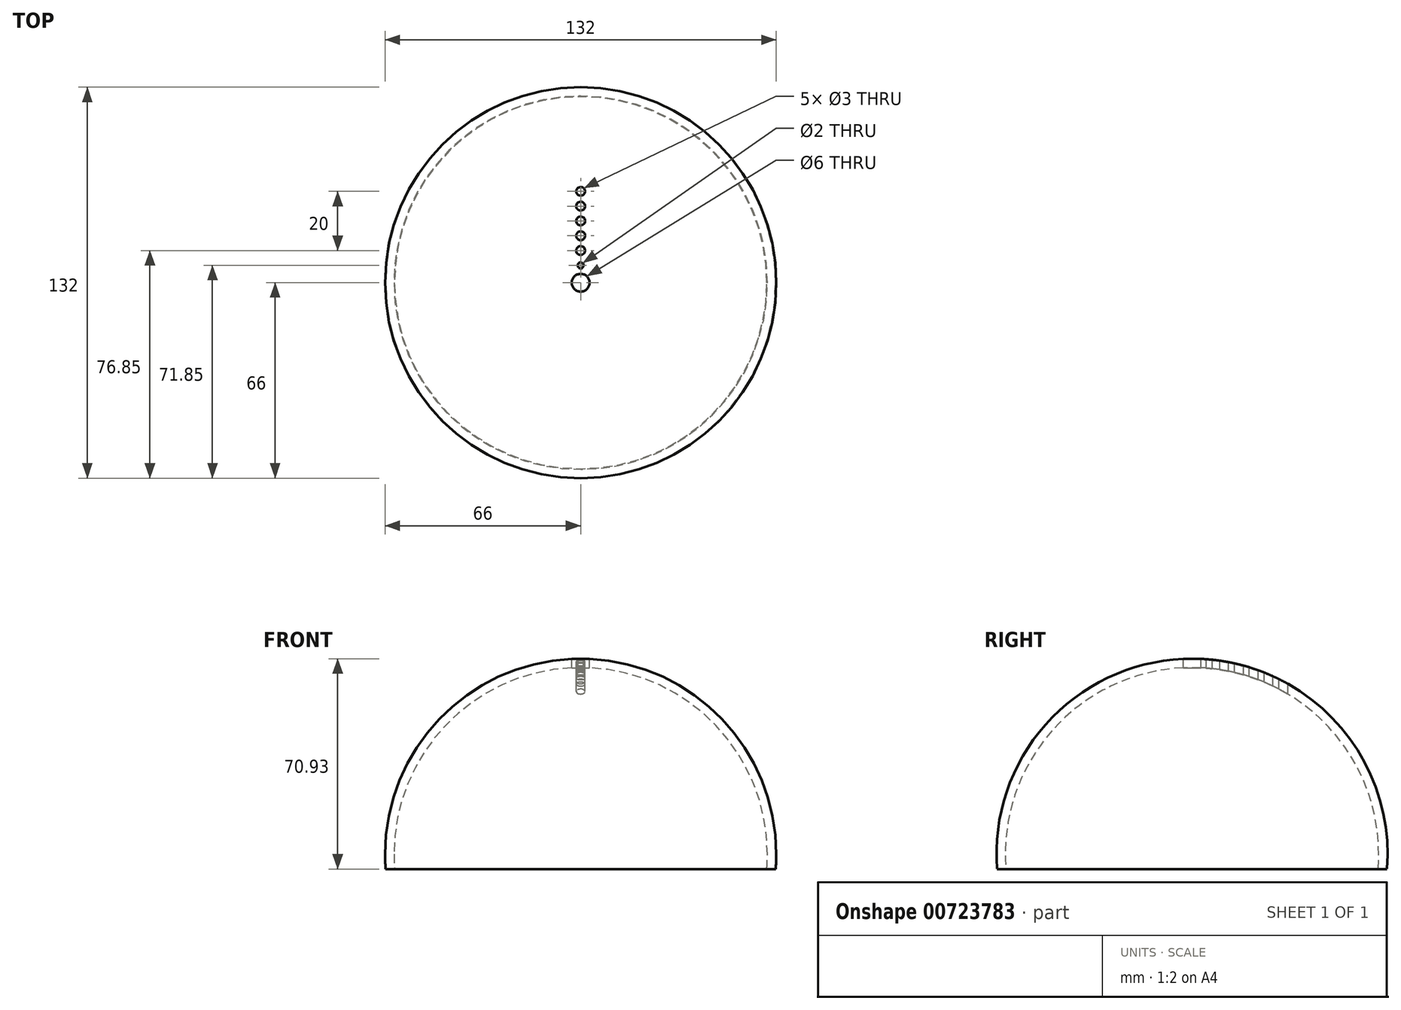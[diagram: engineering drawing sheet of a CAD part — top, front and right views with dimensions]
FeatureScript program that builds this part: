
annotation { "Feature Type Name" : "Feature", "Feature Type Description" : "" }
export const myFeature = defineFeature(function(context is Context, id is Id, definition is map)
    precondition{}
    {
        {
            var Q0;
            Q0=qCreatedBy(makeId("Top.planeOp"),FACE);
            var sketch = newSketch(context, id + "F0", { "sketchPlane" : qUnion([Q0])});
            skArc(sketch, "E0", {"start": v(-66, 0) * mm, "mid": v(0, -66) * mm, "end": v(66, 0) * mm});
            skArc(sketch, "E1.0", {"start": v(-63, 0) * mm, "mid": v(0, -63) * mm, "end": v(63, 0) * mm});
            skLineSegment(sketch, "E2", {"start": v(63, 0) * mm, "end": v(66, 0) * mm});
            skLineSegment(sketch, "E3", {"start": v(-63, 0) * mm, "end": v(-66, 0) * mm});
            skLineSegment(sketch, "E4", {"start": v(63, 0) * mm, "end": v(-63, 0) * mm, "construction": true});
            skSolve(sketch);
        }
        {
            var Q0;
            Q0=makeQuery(id+"F0.imprint","IMPRINT",FACE,{"disambiguationData":[TD([[makeQuery(id+"F0.imprint","IMPRINT",EDGE,{"derivedFrom":sQuery(id+"F0.wireOp",EDGE,"E0")}),1.0]])]});
            var Q1;
            Q1=sQuery(id+"F0.wireOp",EDGE,"E4");
            revolve(context, id + "F1", {"entities" : qUnion([Q0]), "axis" : qUnion([Q1]), "revolveType" : RevolveType.ONE_DIRECTION, "angle" : 360 * degree});
        }
        {
            var Q0;
            Q0=qCreatedBy(makeId("Right.planeOp"),FACE);
            var sketch = newSketch(context, id + "F2", { "sketchPlane" : qUnion([Q0])});
            skLineSegment(sketch, "E5", {"start": v(75, 0) * mm, "end": v(75, -5) * mm});
            skLineSegment(sketch, "E6", {"start": v(75, -5) * mm, "end": v(-75, -5) * mm});
            skLineSegment(sketch, "E7", {"start": v(-75, -5) * mm, "end": v(-75, -68) * mm});
            skLineSegment(sketch, "E8", {"start": v(-75, -68) * mm, "end": v(75, -68) * mm});
            skLineSegment(sketch, "E9", {"start": v(75, -68) * mm, "end": v(75, -5) * mm});
            skSolve(sketch);
        }
        {
            var Q0;
            Q0=makeQuery(id+"F2.imprint","IMPRINT",FACE,{"disambiguationData":[TD([[makeQuery(id+"F2.imprint","IMPRINT",EDGE,{"derivedFrom":sQuery(id+"F2.wireOp",EDGE,"E6")}),1.0]])]});
            extrude(context, id + "F3", {"entities" : qUnion([Q0]), "operationType" : NewBodyOperationType.REMOVE, "oppositeDirection" : true, "depth" : 132 * mm, "symmetric" : true});
        }
        {
            var Q0;
            Q0=qCreatedBy(makeId("Top.planeOp"),FACE);
            cPlane(context, id + "F4", {"entities" : qUnion([Q0]), "cplaneType" : CPlaneType.OFFSET, "offset" : 70 * mm, "width" : 150 * mm, "height" : 150 * mm});
        }
        {
            var Q0;
            Q0=qCreatedBy(id+"F4.planeOp",FACE);
            var sketch = newSketch(context, id + "F5", { "sketchPlane" : qUnion([Q0])});
            skCircle(sketch, "E10", {"center": v(0, 0) * mm, "radius": 33 * mm, "construction": true});
            skCircle(sketch, "E11", {"center": v(0, 30.85) * mm, "radius": 1.5 * mm});
            skCircle(sketch, "E12.2.0.0", {"center": v(-50, 30.85) * mm, "radius": 1 * mm});
            skCircle(sketch, "E13.0.1.0", {"center": v(0, 25.85) * mm, "radius": 1.5 * mm});
            skCircle(sketch, "E13.0.2.0", {"center": v(0, 20.85) * mm, "radius": 1.5 * mm});
            skCircle(sketch, "E13.0.3.0", {"center": v(0, 15.85) * mm, "radius": 1.5 * mm});
            skCircle(sketch, "E13.0.4.0", {"center": v(0, 10.85) * mm, "radius": 1.5 * mm});
            skCircle(sketch, "E13.0.5.0", {"center": v(0, 5.85) * mm, "radius": 1 * mm});
            skLineSegment(sketch, "E13.direction2", {"start": v(0, 30.85) * mm, "end": v(0, 25.85) * mm, "construction": true});
            skSolve(sketch);
        }
        {
            var Q0;
            Q0=makeQuery(id+"F5.imprint","IMPRINT",FACE,{"disambiguationData":[TD([[makeQuery(id+"F5.imprint","IMPRINT",EDGE,{"derivedFrom":sQuery(id+"F5.wireOp",EDGE,"E13.0.5.0")}),1.0]])]});
            var Q1;
            Q1=makeQuery(id+"F5.imprint","IMPRINT",FACE,{"disambiguationData":[TD([[makeQuery(id+"F5.imprint","IMPRINT",EDGE,{"derivedFrom":sQuery(id+"F5.wireOp",EDGE,"E13.0.4.0")}),1.0]])]});
            var Q2;
            Q2=makeQuery(id+"F5.imprint","IMPRINT",FACE,{"disambiguationData":[TD([[makeQuery(id+"F5.imprint","IMPRINT",EDGE,{"derivedFrom":sQuery(id+"F5.wireOp",EDGE,"E13.0.3.0")}),1.0]])]});
            var Q3;
            Q3=makeQuery(id+"F5.imprint","IMPRINT",FACE,{"disambiguationData":[TD([[makeQuery(id+"F5.imprint","IMPRINT",EDGE,{"derivedFrom":sQuery(id+"F5.wireOp",EDGE,"E13.0.2.0")}),1.0]])]});
            var Q4;
            Q4=makeQuery(id+"F5.imprint","IMPRINT",FACE,{"disambiguationData":[TD([[makeQuery(id+"F5.imprint","IMPRINT",EDGE,{"derivedFrom":sQuery(id+"F5.wireOp",EDGE,"E13.0.1.0")}),1.0]])]});
            var Q5;
            Q5=makeQuery(id+"F5.imprint","IMPRINT",FACE,{"disambiguationData":[TD([[makeQuery(id+"F5.imprint","IMPRINT",EDGE,{"derivedFrom":sQuery(id+"F5.wireOp",EDGE,"E11")}),1.0]])]});
            extrude(context, id + "F6", {"entities" : qUnion([Q0, Q1, Q2, Q3, Q4, Q5]), "operationType" : NewBodyOperationType.REMOVE, "oppositeDirection" : true, "depth" : 25 * mm});
        }
        {
            var Q0;
            Q0=qCreatedBy(makeId("Front.planeOp"),FACE);
            var sketch = newSketch(context, id + "F7", { "sketchPlane" : qUnion([Q0])});
            skLineSegment(sketch, "E14", {"start": v(0, 0) * mm, "end": v(0, 82.58) * mm, "construction": true});
            skSolve(sketch);
        }
        {
            var Q0;
            Q0=qCreatedBy(id+"F4.planeOp",FACE);
            var sketch = newSketch(context, id + "F8", { "sketchPlane" : qUnion([Q0])});
            skCircle(sketch, "E15", {"center": v(0, 0) * mm, "radius": 3 * mm});
            skSolve(sketch);
        }
        {
            var Q0;
            Q0=makeQuery(id+"F8.imprint","IMPRINT",FACE,{"disambiguationData":[TD([[makeQuery(id+"F8.imprint","IMPRINT",EDGE,{"derivedFrom":sQuery(id+"F8.wireOp",EDGE,"E15")}),1.0]])]});
            extrude(context, id + "F9", {"entities" : qUnion([Q0]), "operationType" : NewBodyOperationType.REMOVE, "oppositeDirection" : true, "depth" : 25 * mm});
        }
    });
